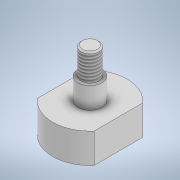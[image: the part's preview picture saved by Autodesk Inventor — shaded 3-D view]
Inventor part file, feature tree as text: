
AUTODESK INVENTOR PART (.ipt)
format: ipt  version: 2021 (Build 250183000, 183)  size: 134,144 bytes
history: native  units: mm
features: sketch x5, extrude x4, chamfer x1, thread x1, hole x1
ambient origin geometry x8: Origin, YZ Plane, XZ Plane, XY Plane, X Axis, Y Axis, Z Axis, Center Point
bodies: Solid1 (feature_tree)
feature tree (12):
  extrude  "Extrusion1"  Depth=10.0mm TaperAngle=0.0deg
  extrude  "Extrusion2"  Depth=7.2mm TaperAngle=0.0deg
  extrude  "Extrusion3"  Depth=9.0mm TaperAngle=0.0deg
  chamfer  "Chamfer1"  Distance=0.5mm Angle=45.0deg
  thread  "Thread1"  [1 undecoded]
  hole  "Hole1"  [1 undecoded]
  extrude  "Extrusion4"  [1 undecoded]
  sketch  "Sketch1"  dims[d0=25.0mm d1=10.0mm d2=0.0mm]
  sketch  "Sketch2"  dims[d3=8.0mm d4=7.2mm d5=0.0mm]
  sketch  "Sketch3"  dims[d6=6.0mm d7=9.0mm d8=0.0mm d9=0.5mm d10=2.0mm d11=45.0deg d12=16.0mm d13=0.0mm]
  sketch  "Sketch4"  dims[d14=6.647mm d15=8.0mm d16=4.0mm d17=2.0mm d18=90.0deg d19=8.0mm d20=20.594885mm d21=19.0mm]
  sketch  "Sketch5"  dims[d22=0.0mm d23=0.0mm]
note: 3 required parameter values undecoded (feature->parameter linkage not recoverable at this tier; creation-order binding heuristic only, values carry confidence <= 0.55)
